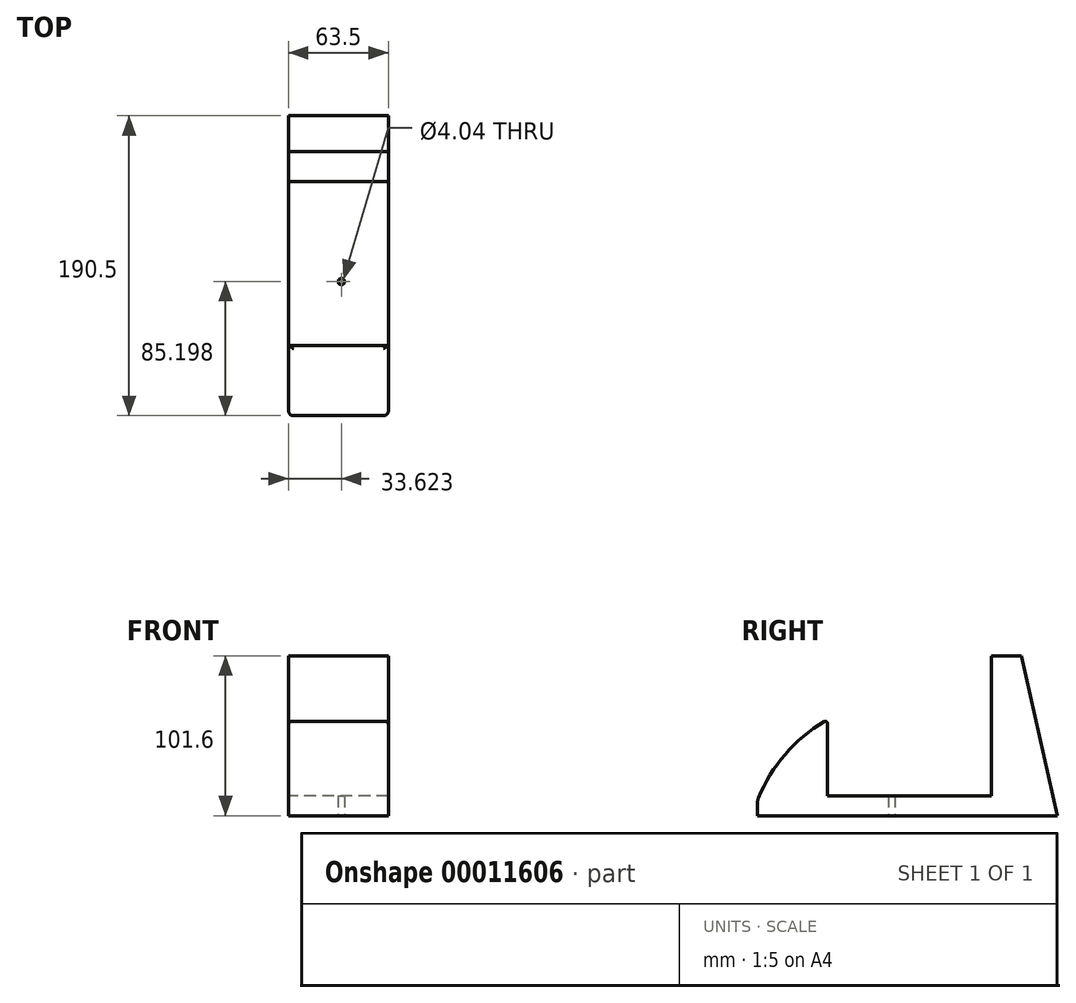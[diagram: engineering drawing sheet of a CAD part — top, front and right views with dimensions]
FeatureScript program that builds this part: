
annotation { "Feature Type Name" : "Feature", "Feature Type Description" : "" }
export const myFeature = defineFeature(function(context is Context, id is Id, definition is map)
    precondition{}
    {
        {
            var Q0;
            Q0=qCreatedBy(makeId("Right.planeOp"),FACE);
            var sketch = newSketch(context, id + "F0", { "sketchPlane" : qUnion([Q0])});
            skLineSegment(sketch, "E0", {"start": v(93.98, 0) * mm, "end": v(-96.52, 0) * mm});
            skLineSegment(sketch, "E1", {"start": v(-52.07, 58.75) * mm, "end": v(-52.07, 12.7) * mm});
            skLineSegment(sketch, "E2", {"start": v(-52.07, 12.7) * mm, "end": v(52.07, 12.7) * mm});
            skLineSegment(sketch, "E3", {"start": v(52.07, 12.7) * mm, "end": v(52.07, 101.6) * mm});
            skLineSegment(sketch, "E4", {"start": v(52.07, 101.6) * mm, "end": v(71.12, 101.6) * mm});
            skLineSegment(sketch, "E5", {"start": v(0, 0) * mm, "end": v(0, 12.7) * mm, "construction": true});
            skLineSegment(sketch, "E6", {"start": v(71.12, 101.6) * mm, "end": v(93.98, 0) * mm});
            skLineSegment(sketch, "E7", {"start": v(-96.52, 0) * mm, "end": v(-96.52, 7.69) * mm});
            skArc(sketch, "E8", {"start": v(-54, 59.84) * mm, "mid": v(-78.82, 38.96) * mm, "end": v(-95.8, 11.32) * mm});
            skPoint(sketch, "E9.visualSharp", {"position": v(-96.52, 9.52) * mm});
            skArc(sketch, "E9.filletArc", {"start": v(-95.8, 11.32) * mm, "mid": v(-96.34, 9.54) * mm, "end": v(-96.52, 7.69) * mm});
            skPoint(sketch, "E10.visualSharp", {"position": v(-52.07, 60.96) * mm});
            skArc(sketch, "E10.filletArc", {"start": v(-52.07, 58.75) * mm, "mid": v(-52.71, 59.85) * mm, "end": v(-54, 59.84) * mm});
            skSolve(sketch);
        }
        {
            var Q0;
            Q0 = qSketchRegion(id + "F0", true);
            extrude(context, id + "F1", {"entities" : qUnion([Q0]), "depth" : 63.5 * mm, "symmetric" : true});
        }
        {
            var Q0;
            Q0=makeQuery(id+"F1.opExtrude","CAP_EDGE",EDGE,{"disambiguationData":[OSD([sQuery(id+"F0.wireOp",EDGE,"E8")])],"isStart":false});
            var Q1;
            Q1=makeQuery(id+"F1.opExtrude","CAP_EDGE",EDGE,{"disambiguationData":[OSD([sQuery(id+"F0.wireOp",EDGE,"E8")])],"isStart":true});
            var Q2;
            Q2=makeQuery(id+"F1.opExtrude","CAP_EDGE",EDGE,{"disambiguationData":[OSD([sQuery(id+"F0.wireOp",EDGE,"E7")])],"isStart":false});
            var Q3;
            Q3=makeQuery(id+"F1.opExtrude","CAP_EDGE",EDGE,{"disambiguationData":[OSD([sQuery(id+"F0.wireOp",EDGE,"E7")])],"isStart":true});
            var Q4;
            Q4=makeQuery(id+"F1.opExtrude","CAP_EDGE",EDGE,{"disambiguationData":[OSD([sQuery(id+"F0.wireOp",EDGE,"E9.filletArc")])],"isStart":true});
            var Q5;
            Q5=makeQuery(id+"F1.opExtrude","CAP_EDGE",EDGE,{"disambiguationData":[OSD([sQuery(id+"F0.wireOp",EDGE,"E9.filletArc")])],"isStart":false});
            fillet(context, id + "F2", {"entities" : qUnion([Q0, Q1, Q2, Q3, Q4, Q5]), "radius" : 3.17 * mm, "allowEdgeOverflow" : false});
        }
        {
            var Q0;
            Q0=makeQuery(id+"F1.opExtrude","SWEPT_FACE",FACE,{"disambiguationData":[OSD([sQuery(id+"F0.wireOp",EDGE,"E2")])]});
            var sketch = newSketch(context, id + "F3", { "sketchPlane" : qUnion([Q0])});
            skPoint(sketch, "E11", {"position": v(1.87, -11.32) * mm});
            skSolve(sketch);
        }
        {
            var Q0;
            Q0=sQuery(id+"F3.wireOp",VERTEX,"E11");
            var Q1;
            Q1=makeQuery(id+"F1.opExtrude","SWEPT_BODY",BODY,{"disambiguationData":[OSD([sQuery(id+"F0.wireOp",EDGE,"E0"),sQuery(id+"F0.wireOp",EDGE,"E1"),sQuery(id+"F0.wireOp",EDGE,"E2"),sQuery(id+"F0.wireOp",EDGE,"E3"),sQuery(id+"F0.wireOp",EDGE,"E4"),sQuery(id+"F0.wireOp",EDGE,"E6"),sQuery(id+"F0.wireOp",EDGE,"E7"),sQuery(id+"F0.wireOp",EDGE,"E8"),sQuery(id+"F0.wireOp",EDGE,"E9.filletArc"),sQuery(id+"F0.wireOp",EDGE,"E10.filletArc")])]});
            hole(context, id + "F4", {"style" : HoleStyle.SIMPLE, "endStyle" : HoleEndStyle.THROUGH, "standardTappedOrClearance" : lookupTablePath({ "standard" : "ANSI", "engagement" : "75%", "pitch" : "32 tpi", "size" : "#10", "type" : "Tapped" }), "standardBlindInLast" : lookupTablePath({ "standard" : "ANSI", "engagement" : "75%", "pitch" : "32 tpi", "size" : "#10", "type" : "Tapped" }), "holeDiameter" : 4.04 * mm, "startFromSketch" : true, "locations" : qUnion([Q0]), "scope" : qUnion([Q1]), "isTappedThrough" : true, "majorDiameter" : 4.83 * mm, "showTappedDepth" : true});
        }
    });
